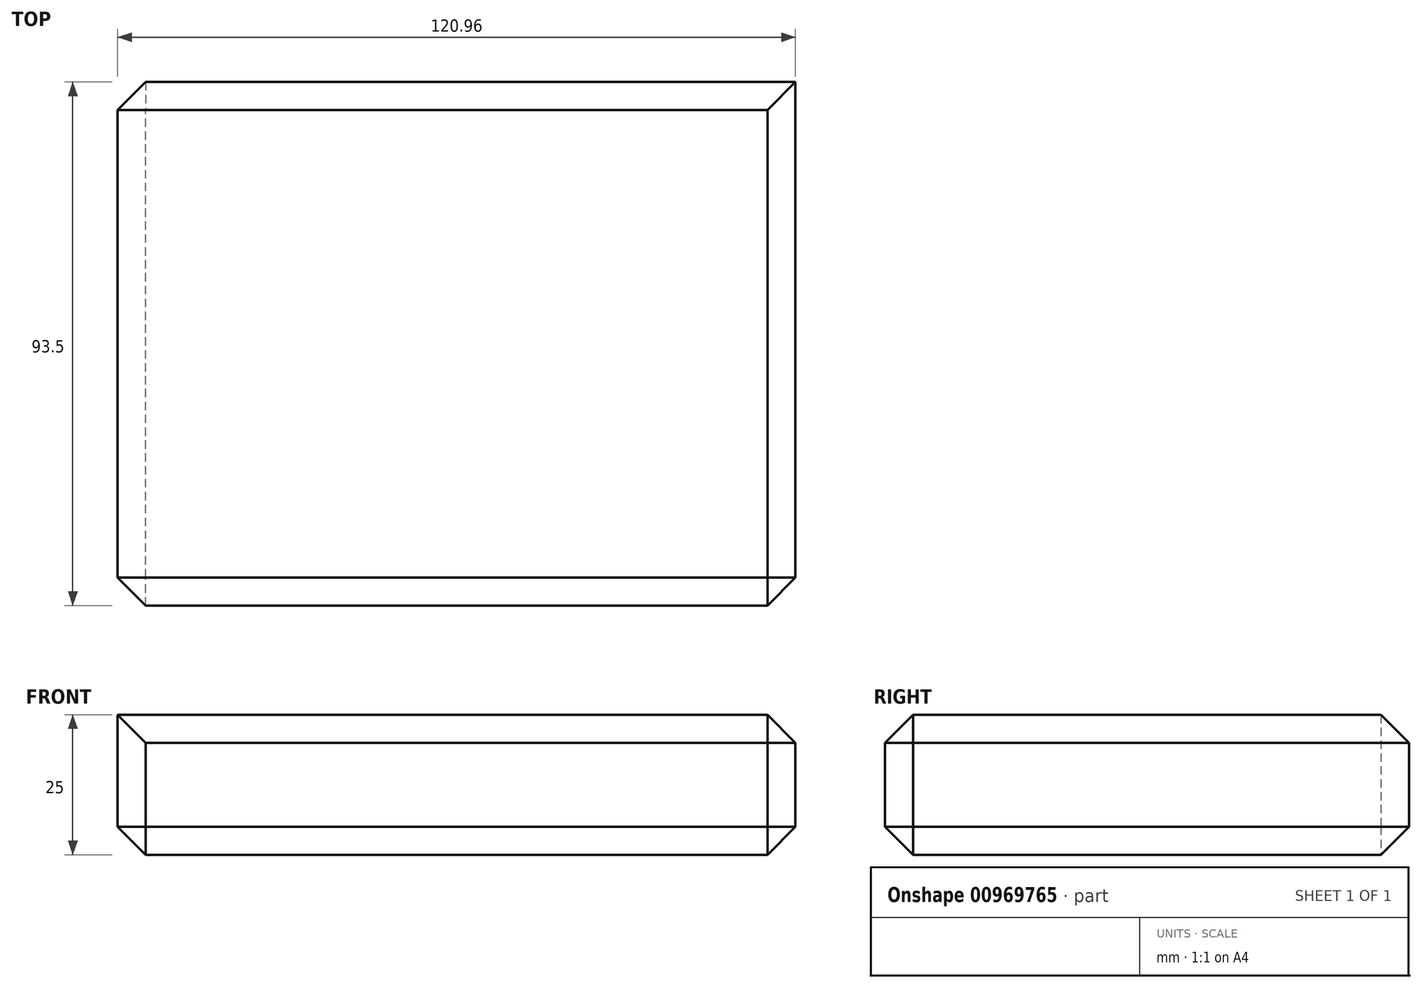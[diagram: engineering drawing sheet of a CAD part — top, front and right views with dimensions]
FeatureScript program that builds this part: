
annotation { "Feature Type Name" : "Feature", "Feature Type Description" : "" }
export const myFeature = defineFeature(function(context is Context, id is Id, definition is map)
    precondition{}
    {
        {
            var Q0;
            Q0=qCreatedBy(makeId("Top.planeOp"),FACE);
            var sketch = newSketch(context, id + "F0", { "sketchPlane" : qUnion([Q0])});
            skLineSegment(sketch, "E0.bottom", {"start": v(-60.48, 46.75) * mm, "end": v(60.48, 46.75) * mm});
            skLineSegment(sketch, "E0.top", {"start": v(-60.48, -46.75) * mm, "end": v(60.48, -46.75) * mm});
            skLineSegment(sketch, "E0.left", {"start": v(-60.48, 46.75) * mm, "end": v(-60.48, -46.75) * mm});
            skLineSegment(sketch, "E0.right", {"start": v(60.48, 46.75) * mm, "end": v(60.48, -46.75) * mm});
            skPoint(sketch, "E0.middle", {"position": v(0, 0) * mm});
            skSolve(sketch);
        }
        {
            var Q0;
            Q0=makeQuery(id+"F0.imprint","IMPRINT",FACE,{"disambiguationData":[TD([[makeQuery(id+"F0.imprint","IMPRINT",EDGE,{"derivedFrom":sQuery(id+"F0.wireOp",EDGE,"E0.bottom")}),-1.0]])]});
            extrude(context, id + "F1", {"entities" : qUnion([Q0]), "depth" : 25 * mm, "offsetDistance" : 25 * mm});
        }
        {
            var Q0;
            Q0=makeQuery(id+"F1.opExtrude","CAP_EDGE",EDGE,{"disambiguationData":[OSD([sQuery(id+"F0.wireOp",EDGE,"E0.top")])],"isStart":false});
            var Q1;
            Q1=makeQuery(id+"F1.opExtrude","CAP_EDGE",EDGE,{"disambiguationData":[OSD([sQuery(id+"F0.wireOp",EDGE,"E0.right")])],"isStart":false});
            var Q2;
            Q2=makeQuery(id+"F1.opExtrude","SWEPT_EDGE",EDGE,{"disambiguationData":[OSD([sQuery(id+"F0.wireOp",EDGE,"E0.top"),sQuery(id+"F0.wireOp",EDGE,"E0.right")])]});
            var Q3;
            Q3=makeQuery(id+"F1.opExtrude","CAP_EDGE",EDGE,{"disambiguationData":[OSD([sQuery(id+"F0.wireOp",EDGE,"E0.top")])],"isStart":true});
            var Q4;
            Q4=makeQuery(id+"F1.opExtrude","CAP_EDGE",EDGE,{"disambiguationData":[OSD([sQuery(id+"F0.wireOp",EDGE,"E0.right")])],"isStart":true});
            var Q5;
            Q5=makeQuery(id+"F1.opExtrude","CAP_EDGE",EDGE,{"disambiguationData":[OSD([sQuery(id+"F0.wireOp",EDGE,"E0.bottom")])],"isStart":false});
            var Q6;
            Q6=makeQuery(id+"F1.opExtrude","CAP_EDGE",EDGE,{"disambiguationData":[OSD([sQuery(id+"F0.wireOp",EDGE,"E0.bottom")])],"isStart":true});
            var Q7;
            Q7=makeQuery(id+"F1.opExtrude","CAP_EDGE",EDGE,{"disambiguationData":[OSD([sQuery(id+"F0.wireOp",EDGE,"E0.left")])],"isStart":true});
            var Q8;
            Q8=makeQuery(id+"F1.opExtrude","SWEPT_EDGE",EDGE,{"disambiguationData":[OSD([sQuery(id+"F0.wireOp",EDGE,"E0.bottom"),sQuery(id+"F0.wireOp",EDGE,"E0.left")])]});
            var Q9;
            Q9=makeQuery(id+"F1.opExtrude","SWEPT_FACE",FACE,{"disambiguationData":[OSD([sQuery(id+"F0.wireOp",EDGE,"E0.top")])]});
            chamfer(context, id + "F2", {"entities" : qUnion([Q0, Q1, Q2, Q3, Q4, Q5, Q6, Q7, Q8, Q9]), "width" : 5 * mm, "tangentPropagation" : true});
        }
    });
